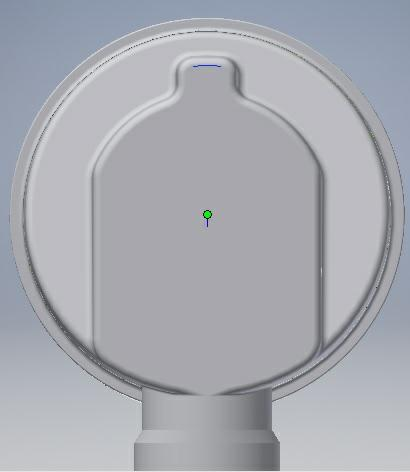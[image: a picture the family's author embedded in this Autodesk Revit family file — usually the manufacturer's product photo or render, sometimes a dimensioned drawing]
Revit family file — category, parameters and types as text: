
# Revit family: S-578
name_source: partatom
category: Uniones de tubería
revit_build: Autodesk Revit 2015 (Build: 20140606_1530(x64)
units: mm (PartAtom-declared; Revit-internal decimal feet)

## types (6) — shared parameters
Aplicación = DUCHAS Ø90
Caudal = 0.6 L/s
D = 40 mm  [stored 0.131234 ft]
DM = 42 mm
Entradas = Ø115 mm
Espesor plato_Max = 27 mm
Espesor plato_Min = 2 mm  [stored 0.00656168 ft]
Fabricante = Jimten
Material = PP (Blanco)
Modelo = S-578
URL = http://www.jimten.com

## per-type parameters (varying)
| type | Comentarios de tipo | Descripción | Material capó | Referencia | Salida | Tubo 40/50 |
| S-578_40_BLANCO | 58 MM DE ALTURA, FACIL INSTALACION GRACIAS A SU SISTEMA DE JUNTAS INTEGRADAS, CON SISTEMA DE BRIDAS METALICAS PARA PLATOS HASTA 26 MM DE ESPESOR POR 3 TORNILLOS, INCLUYE ADAPTADOR A TUBOS DE PVC | SIFON PARA PLATO DE DUCHA JUNTAFIX, SALIDA HORIZONTAL, ALTURA REDUCIDA, CAPO BLANCO | ABS (Blanco) | 012869 | Ø40 MM (HEMBRA) | No |
| S-578_40_ACERO INOX CROMO | 58 MM DE ALTURA, FACIL INSTALACION GRACIAS A SU SISTEMA DE JUNTAS INTEGRADAS, CON SISTEMA DE BRIDAS METALICAS PARA PLATOS HASTA 26 MM DE ESPESOR POR 3 TORNILLOS, INCLUYE ADAPTADOR A TUBOS DE PVC | SIFON PARA PLATO DE DUCHA JUNTAFIX, SALIDA HORIZONTAL, ALTURA REDUCIDA, CAPO EN ACERO INOX CROMO | Acero inox. Cromo | 012519 | Ø40 MM (HEMBRA) | No |
| S-578_40_ACERO INOX SATINADO | 58 MM DE ALTURA, FACIL INSTALACION GRACIAS A SU SISTEMA DE JUNTAS INTEGRADAS, CON SISTEMA DE BRIDAS METALICAS PARA PLATOS HASTA 26 MM DE ESPESOR POR 3 TORNILLOS, INCLUYE ADAPTADOR A TUBOS DE PVC | SIFON PARA PLATO DE DUCHA JUNTAFIX, SALIDA HORIZONTAL, ALTURA REDUCIDA, CAPO EN ACERO INOX SATINADO | Acero inox. Satinado | 012279 | Ø40 MM (HEMBRA) | No |
| S-578_40/50_ACERO INOX SATINADO | 58 MM DE ALTURA, FACIL INSTALACION GRACIAS A SU SISTEMA DE JUNTAS INTEGRADAS, CON SISTEMA DE BRIDAS METALICAS PARA PLATOS HASTA 26 MM DE ESPESOR POR 3 TORNILLOS, INCLUYE ADAPTADOR A TUBOS DE 40/50 | SIFON PARA PLATO DE DUCHA JUNTAFIX, SALIDA HORIZONTAL, ALTURA REDUCIDA, CAPO EN ACERO INOX SATINADO | Acero inox. Satinado | 012299 | Ø40/50 MM (MACHO) | Sí |
| S-578_40/50_ACERO INOX CROMO | 58 MM DE ALTURA, FACIL INSTALACION GRACIAS A SU SISTEMA DE JUNTAS INTEGRADAS, CON SISTEMA DE BRIDAS METALICAS PARA PLATOS HASTA 26 MM DE ESPESOR POR 3 TORNILLOS, INCLUYE ADAPTADOR A TUBOS DE 40/50 | SIFON PARA PLATO DE DUCHA JUNTAFIX, SALIDA HORIZONTAL, ALTURA REDUCIDA, CAPO EN ACERO INOX CROMO | Acero inox. Cromo | 012529 | Ø40/50 MM (MACHO) | Sí |
| S-578_40/50_BLANCO | 58 MM DE ALTURA, FACIL INSTALACION GRACIAS A SU SISTEMA DE JUNTAS INTEGRADAS, CON SISTEMA DE BRIDAS METALICAS PARA PLATOS HASTA 26 MM DE ESPESOR POR 3 TORNILLOS, INCLUYE ADAPTADOR A TUBOS DE 40/50 | SIFON PARA PLATO DE DUCHA JUNTAFIX, SALIDA HORIZONTAL, ALTURA REDUCIDA, CAPO BLANCO | ABS (Blanco) | 012929 | Ø40/50 MM (MACHO) | Sí |

note: [stored X ft] marks values corroborated as IEEE doubles in the binary element streams (Revit-internal decimal feet)

## geometry (parser evidence)
native form markers: Blend x3
no freeform markers — native parametric forms only
